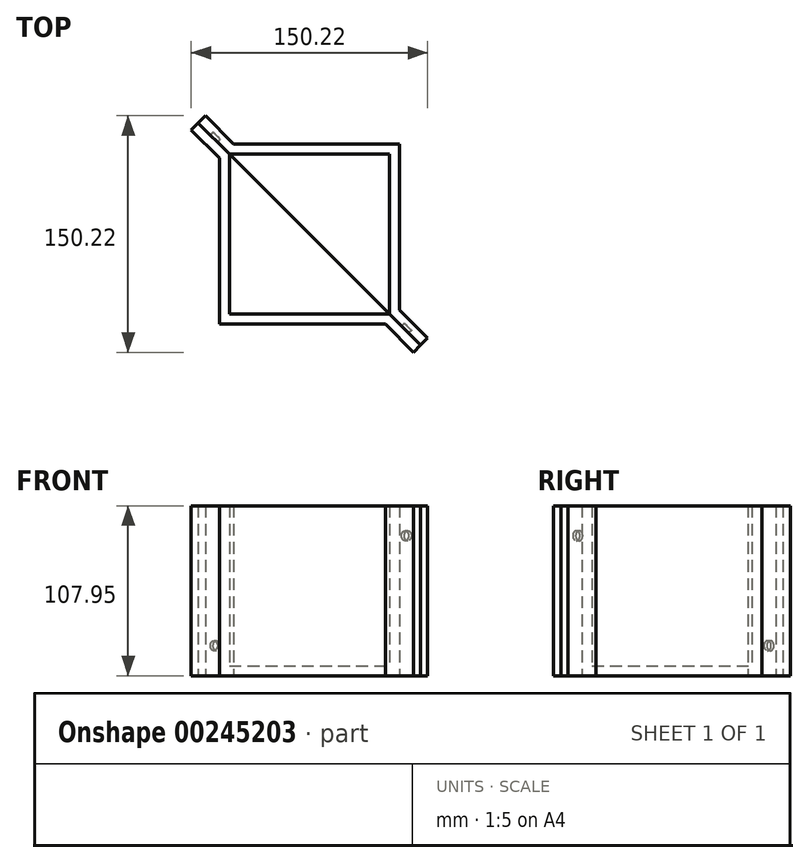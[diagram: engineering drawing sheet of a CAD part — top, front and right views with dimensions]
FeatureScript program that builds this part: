
annotation { "Feature Type Name" : "Feature", "Feature Type Description" : "" }
export const myFeature = defineFeature(function(context is Context, id is Id, definition is map)
    precondition{}
    {
        {
            var Q0;
            Q0=qCreatedBy(makeId("Top.planeOp"),FACE);
            var sketch = newSketch(context, id + "F0", { "sketchPlane" : qUnion([Q0])});
            skLineSegment(sketch, "E0.bottom", {"start": v(0, 0) * mm, "end": v(88.9, 0) * mm});
            skLineSegment(sketch, "E0.top", {"start": v(5.08, 93.98) * mm, "end": v(88.9, 93.98) * mm});
            skLineSegment(sketch, "E0.left", {"start": v(0, 0) * mm, "end": v(0, 88.9) * mm});
            skLineSegment(sketch, "E0.right", {"start": v(93.98, 5.08) * mm, "end": v(93.98, 88.9) * mm});
            skPoint(sketch, "E1.visualSharp", {"position": v(0, 93.98) * mm});
            skArc(sketch, "E1.filletArc", {"start": v(5.08, 93.98) * mm, "mid": v(1.49, 92.5) * mm, "end": v(0, 88.9) * mm});
            skPoint(sketch, "E2.visualSharp", {"position": v(93.98, 93.98) * mm});
            skArc(sketch, "E2.filletArc", {"start": v(93.98, 88.9) * mm, "mid": v(92.5, 92.5) * mm, "end": v(88.9, 93.98) * mm});
            skPoint(sketch, "E3.visualSharp", {"position": v(93.98, 0) * mm});
            skArc(sketch, "E3.filletArc", {"start": v(88.9, 0) * mm, "mid": v(92.5, 1.49) * mm, "end": v(93.98, 5.08) * mm});
            skArc(sketch, "E4.0", {"start": v(5.08, 101.6) * mm, "mid": v(-3.9, 97.88) * mm, "end": v(-7.62, 88.9) * mm});
            skLineSegment(sketch, "E4.1", {"start": v(-7.62, -7.62) * mm, "end": v(-7.62, 88.9) * mm});
            skArc(sketch, "E4.2", {"start": v(101.6, 88.9) * mm, "mid": v(97.88, 97.88) * mm, "end": v(88.9, 101.6) * mm});
            skLineSegment(sketch, "E4.3", {"start": v(101.6, 5.08) * mm, "end": v(101.6, 88.9) * mm});
            skArc(sketch, "E4.4", {"start": v(88.9, -7.62) * mm, "mid": v(97.88, -3.9) * mm, "end": v(101.6, 5.08) * mm});
            skLineSegment(sketch, "E4.5", {"start": v(5.08, 101.6) * mm, "end": v(88.9, 101.6) * mm});
            skLineSegment(sketch, "E4.6", {"start": v(-7.62, -7.62) * mm, "end": v(88.9, -7.62) * mm});
            skSolve(sketch);
        }
        {
            var Q0;
            Q0=qCreatedBy(makeId("Top.planeOp"),FACE);
            cPlane(context, id + "F1", {"entities" : qUnion([Q0]), "cplaneType" : CPlaneType.OFFSET, "offset" : 101.6 * mm, "width" : 152.4 * mm, "height" : 152.4 * mm});
        }
        {
            var Q0;
            Q0=qCreatedBy(makeId("Top.planeOp"),FACE);
            cPlane(context, id + "F2", {"entities" : qUnion([Q0]), "cplaneType" : CPlaneType.OFFSET, "offset" : 6.35 * mm, "oppositeDirection" : true, "width" : 152.4 * mm, "height" : 152.4 * mm});
        }
        {
            var Q0;
            Q0=qCreatedBy(id+"F2.planeOp",FACE);
            var sketch = newSketch(context, id + "F3", { "sketchPlane" : qUnion([Q0])});
            skLineSegment(sketch, "E5.bottom", {"start": v(0, 0) * mm, "end": v(101.6, 0) * mm});
            skLineSegment(sketch, "E5.top", {"start": v(0, 101.6) * mm, "end": v(101.6, 101.6) * mm});
            skLineSegment(sketch, "E5.left", {"start": v(0, 0) * mm, "end": v(0, 101.6) * mm});
            skLineSegment(sketch, "E5.right", {"start": v(101.6, 0) * mm, "end": v(101.6, 101.6) * mm});
            skLineSegment(sketch, "E6.0", {"start": v(2.63, 107.95) * mm, "end": v(107.95, 107.95) * mm});
            skLineSegment(sketch, "E6.1", {"start": v(-6.35, -6.35) * mm, "end": v(-6.35, 98.97) * mm});
            skLineSegment(sketch, "E6.2", {"start": v(-6.35, -6.35) * mm, "end": v(98.97, -6.35) * mm});
            skLineSegment(sketch, "E6.3", {"start": v(107.95, 2.63) * mm, "end": v(107.95, 107.95) * mm});
            skLineSegment(sketch, "E7", {"start": v(107.95, -6.35) * mm, "end": v(-6.35, 107.95) * mm});
            skLineSegment(sketch, "E8", {"start": v(107.95, 107.95) * mm, "end": v(-6.35, -6.35) * mm, "construction": true});
            skLineSegment(sketch, "E9", {"start": v(-6.35, 107.95) * mm, "end": v(-19.82, 121.42) * mm, "construction": true});
            skLineSegment(sketch, "E10", {"start": v(-19.82, 121.42) * mm, "end": v(-15.33, 125.91) * mm});
            skLineSegment(sketch, "E11.0", {"start": v(2.63, 107.95) * mm, "end": v(-15.33, 125.91) * mm});
            skLineSegment(sketch, "E12.MirrorCS", {"start": v(-19.82, 121.42) * mm, "end": v(-24.31, 116.93) * mm});
            skLineSegment(sketch, "E13.MirrorCS", {"start": v(-6.35, 98.97) * mm, "end": v(-24.31, 116.93) * mm});
            skLineSegment(sketch, "E14.MirrorCS", {"start": v(98.97, -6.35) * mm, "end": v(116.93, -24.31) * mm});
            skLineSegment(sketch, "E15.MirrorCS", {"start": v(121.42, -19.82) * mm, "end": v(116.93, -24.31) * mm});
            skLineSegment(sketch, "E16.MirrorCS", {"start": v(121.42, -19.82) * mm, "end": v(125.91, -15.33) * mm});
            skLineSegment(sketch, "E17.MirrorCS", {"start": v(107.95, 2.63) * mm, "end": v(125.91, -15.33) * mm});
            skLineSegment(sketch, "E18", {"start": v(-19.82, 121.42) * mm, "end": v(0, 101.6) * mm});
            skLineSegment(sketch, "E19", {"start": v(101.6, 0) * mm, "end": v(121.42, -19.82) * mm});
            skSolve(sketch);
        }
        {
            var Q0;
            Q0=makeQuery(id+"F3.imprint","IMPRINT",FACE,{"disambiguationData":[TD([[makeQuery(id+"F3.imprint","IMPRINT",EDGE,{"derivedFrom":sQuery(id+"F3.wireOp",EDGE,"E5.bottom")}),1.0]])]});
            var Q1;
            {var subQ5=sQuery(id+"F3.wireOp",EDGE,"E5.bottom");Q1=makeQuery(id+"F3.imprint","IMPRINT",FACE,{"disambiguationData":[TD([[makeQuery(id+"F3.imprint","IMPRINT",EDGE,{"derivedFrom":subQ5}),-1.0]])]});}
            extrude(context, id + "F4", {"entities" : qUnion([Q0, Q1]), "depth" : 6.35 * mm});
        }
        {
            var Q0;
            {var subQ5=sQuery(id+"F3.wireOp",EDGE,"E5.bottom");Q0=makeQuery(id+"F3.imprint","IMPRINT",FACE,{"disambiguationData":[TD([[makeQuery(id+"F3.imprint","IMPRINT",EDGE,{"derivedFrom":subQ5}),-1.0]])]});}
            extrude(context, id + "F5", {"entities" : qUnion([Q0]), "depth" : 107.95 * mm});
        }
        {
            var Q0;
            Q0=makeQuery(id+"F5.opExtrude","SWEPT_BODY",BODY,{"disambiguationData":[OSD([sQuery(id+"F3.wireOp",EDGE,"E5.bottom"),sQuery(id+"F3.wireOp",EDGE,"E5.left"),sQuery(id+"F3.wireOp",EDGE,"E6.1"),sQuery(id+"F3.wireOp",EDGE,"E6.2"),sQuery(id+"F3.wireOp",EDGE,"E12.MirrorCS"),sQuery(id+"F3.wireOp",EDGE,"E13.MirrorCS"),sQuery(id+"F3.wireOp",EDGE,"E14.MirrorCS"),sQuery(id+"F3.wireOp",EDGE,"E15.MirrorCS"),sQuery(id+"F3.wireOp",EDGE,"E18"),sQuery(id+"F3.wireOp",EDGE,"E19")])]});
            var Q1;
            Q1=makeQuery(id+"F4.opExtrude","SWEPT_BODY",BODY,{"disambiguationData":[OSD([sQuery(id+"F3.wireOp",EDGE,"E6.1"),sQuery(id+"F3.wireOp",EDGE,"E6.2"),sQuery(id+"F3.wireOp",EDGE,"E7"),sQuery(id+"F3.wireOp",EDGE,"E12.MirrorCS"),sQuery(id+"F3.wireOp",EDGE,"E13.MirrorCS"),sQuery(id+"F3.wireOp",EDGE,"E14.MirrorCS"),sQuery(id+"F3.wireOp",EDGE,"E15.MirrorCS"),sQuery(id+"F3.wireOp",EDGE,"E18"),sQuery(id+"F3.wireOp",EDGE,"E19")])]});
            booleanBodies(context, id + "F6", {"operationType" : BooleanOperationType.UNION, "tools" : qUnion([Q0, Q1])});
        }
        {
            var Q0;
            Q0=makeQuery(id+"F5.opExtrude","CAP_VERTEX",VERTEX,{"disambiguationData":[OSD([sQuery(id+"F3.wireOp",EDGE,"E15.MirrorCS"),sQuery(id+"F3.wireOp",EDGE,"E16.MirrorCS"),sQuery(id+"F3.wireOp",EDGE,"E19")])],"isStart":false});
            var Q1;
            {var subQ0=sQuery(id+"F3.wireOp",EDGE,"E19");var subQ1=sQuery(id+"F3.wireOp",EDGE,"E18");Q1=makeQuery(id+"F6.opBoolean","MERGE",FACE,{"derivedFrom":[makeQuery(id+"F4.opExtrude","SWEPT_FACE",FACE,{"disambiguationData":[OSD([sQuery(id+"F3.wireOp",EDGE,"E7"),subQ1,subQ0])]}),makeQuery(id+"F5.opExtrude","SWEPT_FACE",FACE,{"disambiguationData":[OSD([subQ1])]}),makeQuery(id+"F5.opExtrude","SWEPT_FACE",FACE,{"disambiguationData":[OSD([subQ0])]})]});}
            cPlane(context, id + "F7", {"entities" : qUnion([Q0, Q1]), "cplaneType" : CPlaneType.PLANE_POINT, "offset" : 25.4 * mm, "width" : 152.4 * mm, "height" : 152.4 * mm});
        }
        {
            var Q0;
            Q0=qCreatedBy(id+"F7.planeOp",FACE);
            var sketch = newSketch(context, id + "F8", { "sketchPlane" : qUnion([Q0])});
            skLineSegment(sketch, "E20", {"start": v(-85.86, 101.6) * mm, "end": v(-85.86, -6.35) * mm, "construction": true});
            skCircle(sketch, "E21", {"center": v(-85.86, 82.55) * mm, "radius": 3.18 * mm});
            skPoint(sketch, "E22", {"position": v(-85.86, 47.62) * mm});
            skLineSegment(sketch, "E23", {"start": v(-98.62, 47.62) * mm, "end": v(-85.86, 47.62) * mm, "construction": true});
            skCircle(sketch, "E24.MirrorC", {"center": v(-85.86, 12.7) * mm, "radius": 3.18 * mm});
            skLineSegment(sketch, "E25", {"start": v(0, 0) * mm, "end": v(0, 153.64) * mm});
            skCircle(sketch, "E26.MirrorC", {"center": v(85.86, 82.55) * mm, "radius": 3.18 * mm});
            skCircle(sketch, "E27.MirrorC", {"center": v(85.86, 12.7) * mm, "radius": 3.18 * mm});
            skSolve(sketch);
        }
        {
            var Q0;
            Q0=makeQuery(id+"F8.imprint","IMPRINT",FACE,{"disambiguationData":[TD([[makeQuery(id+"F8.imprint","IMPRINT",EDGE,{"derivedFrom":sQuery(id+"F8.wireOp",EDGE,"E26.MirrorC")}),-1.0]])]});
            var Q1;
            Q1=makeQuery(id+"F8.imprint","IMPRINT",FACE,{"disambiguationData":[TD([[makeQuery(id+"F8.imprint","IMPRINT",EDGE,{"derivedFrom":sQuery(id+"F8.wireOp",EDGE,"E27.MirrorC")}),1.0]])]});
            var Q2;
            Q2=makeQuery(id+"F8.imprint","IMPRINT",FACE,{"disambiguationData":[TD([[makeQuery(id+"F8.imprint","IMPRINT",EDGE,{"derivedFrom":sQuery(id+"F8.wireOp",EDGE,"E21")}),1.0]])]});
            var Q3;
            Q3=makeQuery(id+"F8.imprint","IMPRINT",FACE,{"disambiguationData":[TD([[makeQuery(id+"F8.imprint","IMPRINT",EDGE,{"derivedFrom":sQuery(id+"F8.wireOp",EDGE,"E24.MirrorC")}),-1.0]])]});
            extrude(context, id + "F9", {"entities" : qUnion([Q0, Q1, Q2, Q3]), "operationType" : NewBodyOperationType.ADD, "depth" : 2.54 * mm});
        }
        {
            var Q0;
            Q0=makeQuery(id+"F5.opExtrude","SWEPT_BODY",BODY,{"disambiguationData":[OSD([sQuery(id+"F3.wireOp",EDGE,"E5.bottom"),sQuery(id+"F3.wireOp",EDGE,"E5.left"),sQuery(id+"F3.wireOp",EDGE,"E6.1"),sQuery(id+"F3.wireOp",EDGE,"E6.2"),sQuery(id+"F3.wireOp",EDGE,"E12.MirrorCS"),sQuery(id+"F3.wireOp",EDGE,"E13.MirrorCS"),sQuery(id+"F3.wireOp",EDGE,"E14.MirrorCS"),sQuery(id+"F3.wireOp",EDGE,"E15.MirrorCS"),sQuery(id+"F3.wireOp",EDGE,"E18"),sQuery(id+"F3.wireOp",EDGE,"E19")])]});
            var Q1;
            Q1=qCreatedBy(id+"F7.planeOp",FACE);
            mirror(context, id + "F10", {"entities" : qUnion([Q0]), "mirrorPlane" : qUnion([Q1])});
        }
        {
            var Q0;
            Q0=makeQuery(id+"F5.opExtrude","SWEPT_BODY",BODY,{"disambiguationData":[OSD([sQuery(id+"F3.wireOp",EDGE,"E5.bottom"),sQuery(id+"F3.wireOp",EDGE,"E5.left"),sQuery(id+"F3.wireOp",EDGE,"E6.1"),sQuery(id+"F3.wireOp",EDGE,"E6.2"),sQuery(id+"F3.wireOp",EDGE,"E12.MirrorCS"),sQuery(id+"F3.wireOp",EDGE,"E13.MirrorCS"),sQuery(id+"F3.wireOp",EDGE,"E14.MirrorCS"),sQuery(id+"F3.wireOp",EDGE,"E15.MirrorCS"),sQuery(id+"F3.wireOp",EDGE,"E18"),sQuery(id+"F3.wireOp",EDGE,"E19")])]});
            var Q1;
            Q1=makeQuery(id+"F10.opPattern","COPY",BODY,{"derivedFrom":makeQuery(id+"F5.opExtrude","SWEPT_BODY",BODY,{"disambiguationData":[OSD([sQuery(id+"F3.wireOp",EDGE,"E5.bottom"),sQuery(id+"F3.wireOp",EDGE,"E5.left"),sQuery(id+"F3.wireOp",EDGE,"E6.1"),sQuery(id+"F3.wireOp",EDGE,"E6.2"),sQuery(id+"F3.wireOp",EDGE,"E12.MirrorCS"),sQuery(id+"F3.wireOp",EDGE,"E13.MirrorCS"),sQuery(id+"F3.wireOp",EDGE,"E14.MirrorCS"),sQuery(id+"F3.wireOp",EDGE,"E15.MirrorCS"),sQuery(id+"F3.wireOp",EDGE,"E18"),sQuery(id+"F3.wireOp",EDGE,"E19")])]}),"instanceName":"1"});
            booleanBodies(context, id + "F11", {"operationType" : BooleanOperationType.SUBTRACTION, "tools" : qUnion([Q0]), "targets" : qUnion([Q1]), "keepTools" : true});
        }
    });
